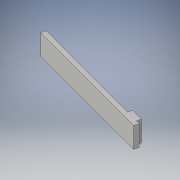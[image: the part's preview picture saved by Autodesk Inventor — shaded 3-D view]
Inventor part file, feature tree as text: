
AUTODESK INVENTOR PART (.ipt)
format: ipt  version: 2016 SP2 (Build 200236200, 236)  size: 98,816 bytes
history: native  units: mm
features: reference x5, extrude x1, sketch x1
ambient origin geometry x8: Origin, YZ Plane, XZ Plane, XY Plane, X Axis, Y Axis, Z Axis, Center Point
bodies: Volumenkörper1 (feature_tree)
feature tree (7):
  extrude  "Extrusion1"  Depth=8.0mm
  sketch  "Skizze1"  dims[d0=51.0mm d2=2.0mm d3=8.0mm d4=0.0mm d5=0.1mm]
  reference  "Referenz1"
  reference  "Referenz2"
  reference  "Referenz3"
  reference  "Referenz4"
  reference  "Referenz5"
